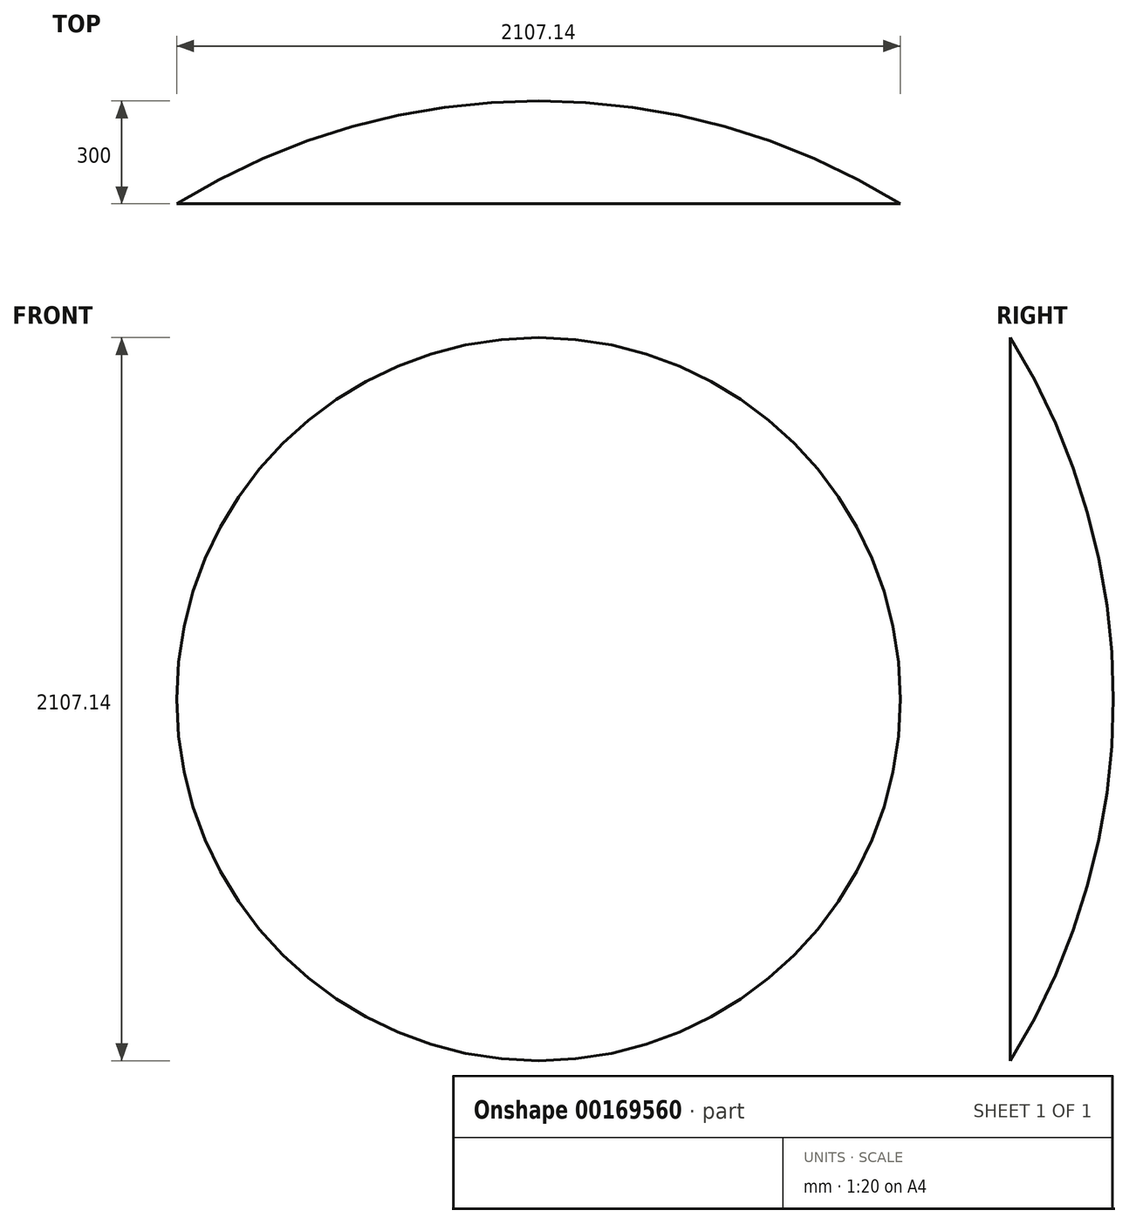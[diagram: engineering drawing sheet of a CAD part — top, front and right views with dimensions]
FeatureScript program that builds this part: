
annotation { "Feature Type Name" : "Feature", "Feature Type Description" : "" }
export const myFeature = defineFeature(function(context is Context, id is Id, definition is map)
    precondition{}
    {
        {
            var Q0;
            Q0=qCreatedBy(makeId("Top.planeOp"),FACE);
            var sketch = newSketch(context, id + "F0", { "sketchPlane" : qUnion([Q0])});
            skArc(sketch, "E0", {"start": v(2000, 0) * mm, "mid": v(0, 2000) * mm, "end": v(-2000, 0) * mm});
            skLineSegment(sketch, "E1", {"start": v(0, 0) * mm, "end": v(-2000, 0) * mm});
            skLineSegment(sketch, "E2", {"start": v(-2000, 0) * mm, "end": v(2000, 0) * mm});
            skSolve(sketch);
        }
        {
            var Q0;
            {var subQ0=sQuery(id+"F0.wireOp",EDGE,"E0");Q0=makeQuery(id+"F0.imprint","IMPRINT",FACE,{"disambiguationData":[TD([[makeQuery(id+"F0.imprint","IMPRINT",EDGE,{"derivedFrom":subQ0}),1.0]])]});}
            var Q1;
            Q1=sQuery(id+"F0.wireOp",EDGE,"E2");
            revolve(context, id + "F1", {"entities" : qUnion([Q0]), "axis" : qUnion([Q1]), "revolveType" : RevolveType.FULL});
        }
        {
            var Q0;
            Q0=qCreatedBy(makeId("Top.planeOp"),FACE);
            var sketch = newSketch(context, id + "F2", { "sketchPlane" : qUnion([Q0])});
            skLineSegment(sketch, "E3.bottom", {"start": v(2500, -1700) * mm, "end": v(-2500, -1700) * mm});
            skLineSegment(sketch, "E3.top", {"start": v(2500, 1700) * mm, "end": v(-2500, 1700) * mm});
            skLineSegment(sketch, "E3.left", {"start": v(2500, -1700) * mm, "end": v(2500, 1700) * mm});
            skLineSegment(sketch, "E3.right", {"start": v(-2500, -1700) * mm, "end": v(-2500, 1700) * mm});
            skPoint(sketch, "E3.middle", {"position": v(0, 0) * mm});
            skLineSegment(sketch, "E4.bottom", {"start": v(-2500, -1700) * mm, "end": v(2500, -1700) * mm});
            skLineSegment(sketch, "E4.top", {"start": v(-2500, -2700) * mm, "end": v(2500, -2700) * mm});
            skLineSegment(sketch, "E4.left", {"start": v(-2500, -1700) * mm, "end": v(-2500, -2700) * mm});
            skLineSegment(sketch, "E4.right", {"start": v(2500, -1700) * mm, "end": v(2500, -2700) * mm});
            skSolve(sketch);
        }
        {
            var Q0;
            Q0=qCreatedBy(makeId("Top.planeOp"),FACE);
            var sketch = newSketch(context, id + "F3", { "sketchPlane" : qUnion([Q0])});
            skLineSegment(sketch, "E5.bottom", {"start": v(-2500, 1700) * mm, "end": v(2500, 1700) * mm});
            skLineSegment(sketch, "E5.top", {"start": v(-2500, -1700) * mm, "end": v(2500, -1700) * mm});
            skLineSegment(sketch, "E5.left", {"start": v(-2500, 1700) * mm, "end": v(-2500, -1700) * mm});
            skLineSegment(sketch, "E5.right", {"start": v(2500, 1700) * mm, "end": v(2500, -1700) * mm});
            skPoint(sketch, "E5.middle", {"position": v(0, 0) * mm});
            skLineSegment(sketch, "E6.top", {"start": v(-2500, -2700) * mm, "end": v(2500, -2700) * mm});
            skLineSegment(sketch, "E6.left", {"start": v(-2500, -1700) * mm, "end": v(-2500, -2700) * mm});
            skLineSegment(sketch, "E6.right", {"start": v(2500, -1700) * mm, "end": v(2500, -2700) * mm});
            skSolve(sketch);
        }
        {
            var Q0;
            Q0 = qSketchRegion(id + "F2", true);
            extrude(context, id + "F4", {"entities" : qUnion([Q0]), "operationType" : NewBodyOperationType.REMOVE, "endBound" : BoundingType.THROUGH_ALL, "oppositeDirection" : true, "depth" : 25 * mm});
        }
        {
            var Q0;
            Q0 = qSketchRegion(id + "F3", true);
            extrude(context, id + "F5", {"entities" : qUnion([Q0]), "operationType" : NewBodyOperationType.REMOVE, "endBound" : BoundingType.THROUGH_ALL, "depth" : 25 * mm});
        }
    });
